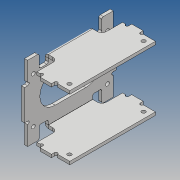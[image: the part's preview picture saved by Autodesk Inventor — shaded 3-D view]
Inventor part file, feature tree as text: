
AUTODESK INVENTOR PART (.ipt)
format: ipt  version: 2017 (Build 210142000, 142)  size: 366,080 bytes
history: native  units: mm
features: other x4, sketch x1, extrude x1
ambient origin geometry x8: Origin, YZ Plane, XZ Plane, XY Plane, X Axis, Y Axis, Z Axis, Center Point
bodies: Body1 (feature_tree)
feature tree (6):
  other  "Sólido1"
  sketch  "Boceto1"  dims[d0=4.0mm d1=40.0mm d2=2.0mm d5=2.0mm d9=15.0mm d10=20.0mm d11=75.8mm d13=120.0mm d14=58.0mm d15=23.0mm d16=4.0mm d17=4.0mm d18=0.0mm d19=4.0mm d20=2.0mm d21=8.0mm d22=4.0mm d23=90.0deg d24=0.1mm d25=4.0mm d26=2.0mm d27=8.0mm d28=4.0mm d29=90.0deg d30=0.1mm d31=8.0mm d32=7.5mm d33=15.0mm d34=5.0mm d35=10.0mm d36=7.5mm d37=40.0mm d38=20.0mm d39=12.0mm d40=4.0mm d41=6.0mm d42=2.0mm d43=6.0mm]
  extrude  "Extrusión1"  Depth=40.0mm
  other  "Pliegue1"
  other  "Pliegue2"
  other  "Definición1"
